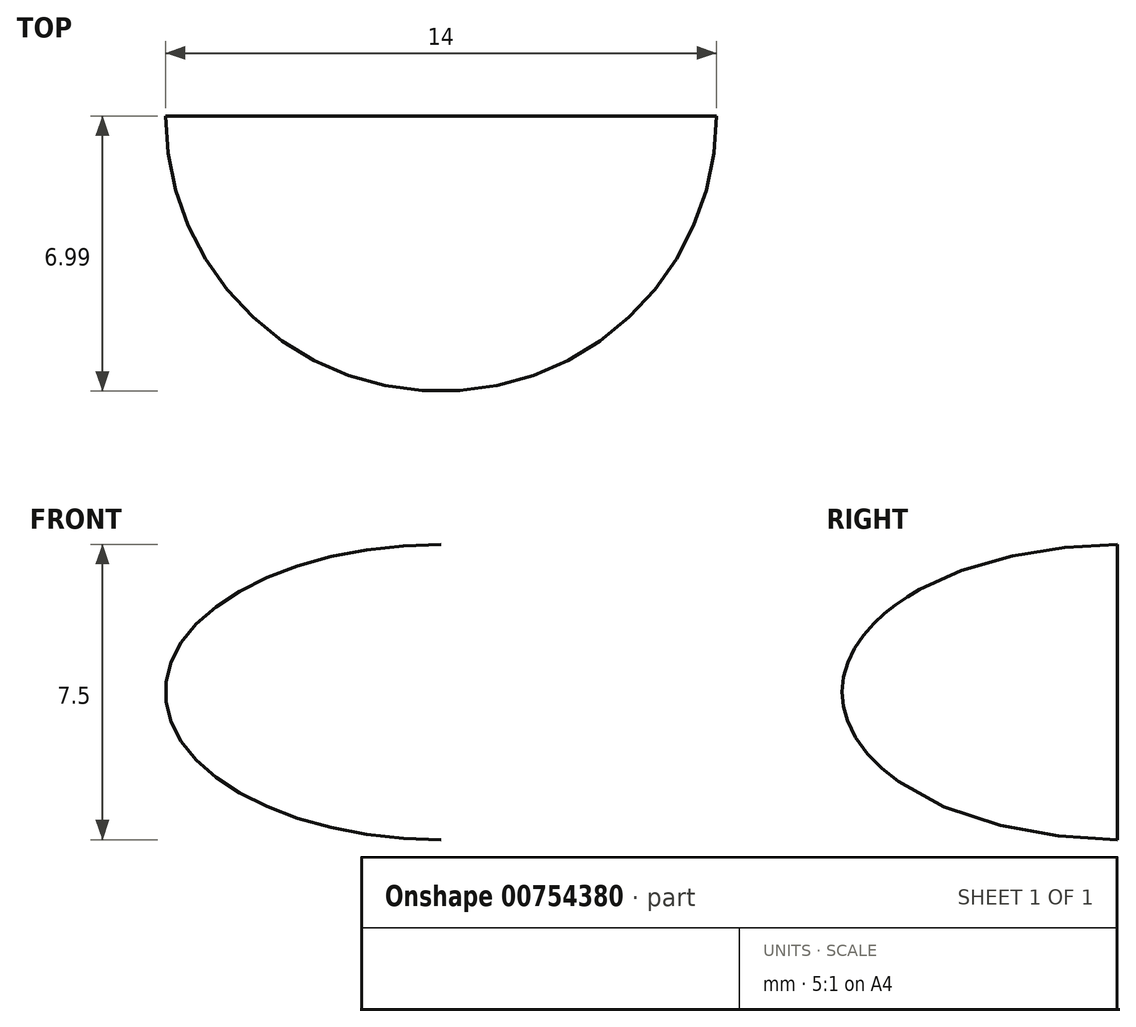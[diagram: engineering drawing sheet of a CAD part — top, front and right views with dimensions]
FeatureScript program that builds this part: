
annotation { "Feature Type Name" : "Feature", "Feature Type Description" : "" }
export const myFeature = defineFeature(function(context is Context, id is Id, definition is map)
    precondition{}
    {
        {
            var Q0;
            Q0=qCreatedBy(makeId("Front.planeOp"),FACE);
            var sketch = newSketch(context, id + "F0", { "sketchPlane" : qUnion([Q0])});
            skEllipticalArc(sketch, "E0", {});
            skLineSegment(sketch, "E1", {"start": v(0, 3.75) * mm, "end": v(0, -3.75) * mm});
            const initialGuessF0  = {"E0": [0, 0, -1, 0, 0.007, 0.00375, 4.71238898038469, 1.5707963267948966]};
            skSetInitialGuess(sketch, initialGuessF0);
            skSolve(sketch);
        }
        {
            var Q0;
            Q0=makeQuery(id+"F0.imprint","IMPRINT",FACE,{"disambiguationData":[TD([[makeQuery(id+"F0.imprint","IMPRINT",EDGE,{"derivedFrom":sQuery(id+"F0.wireOp",EDGE,"E0")}),1.0]])]});
            var Q1;
            Q1=sQuery(id+"F0.wireOp",EDGE,"E1");
            revolve(context, id + "F1", {"surfaceOperationType" : NewSurfaceOperationType.NEW, "entities" : qUnion([Q0]), "axis" : qUnion([Q1]), "revolveType" : RevolveType.ONE_DIRECTION, "oppositeDirection" : true, "angle" : 180 * degree});
        }
    });
